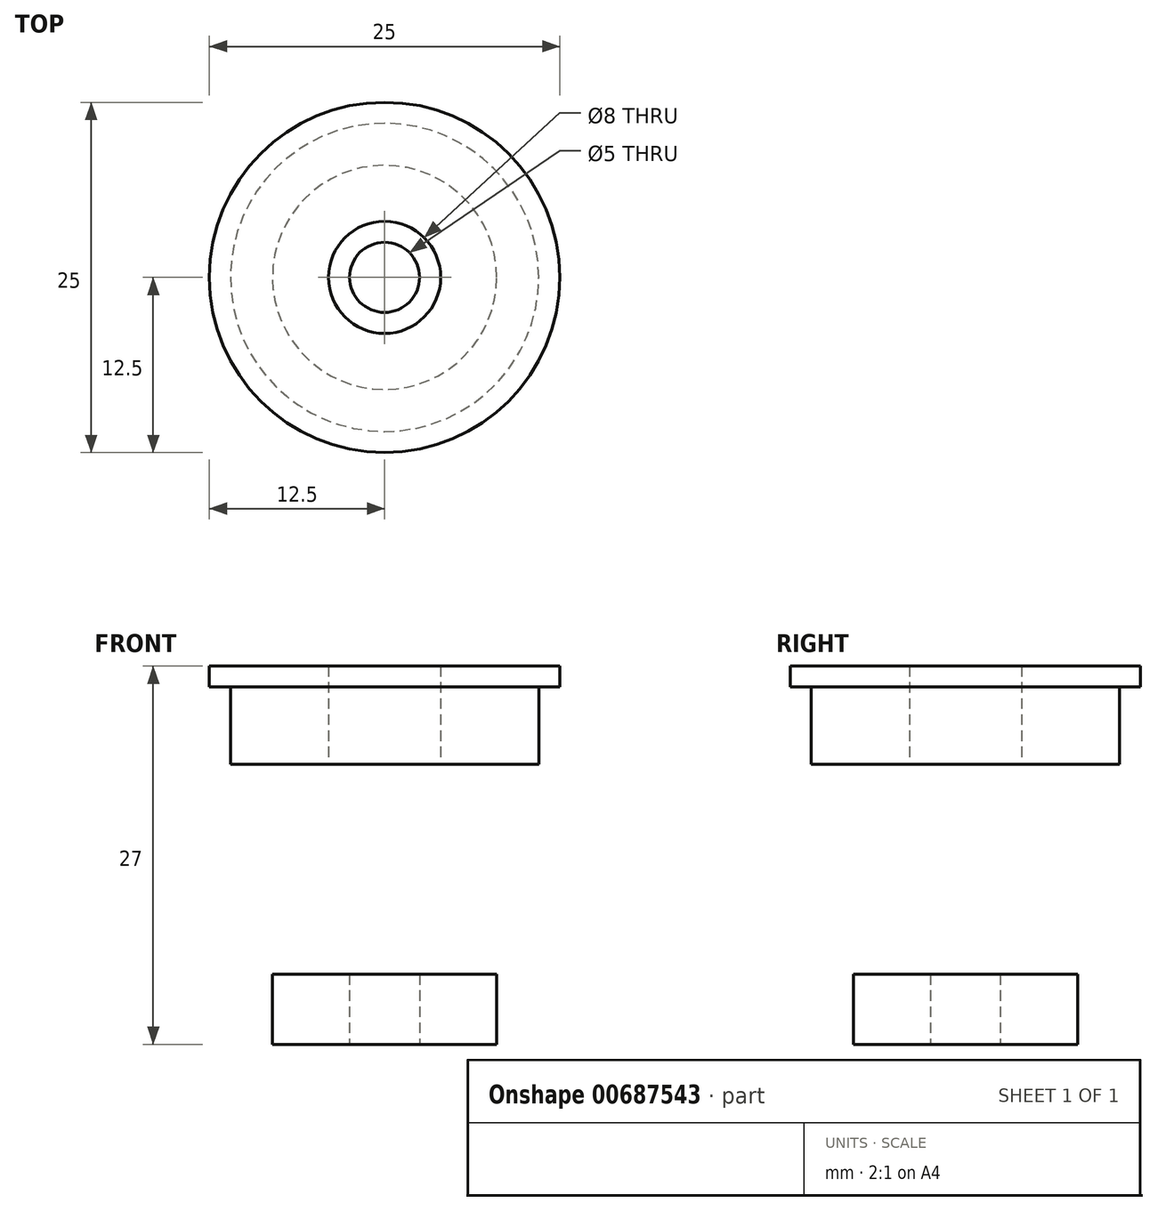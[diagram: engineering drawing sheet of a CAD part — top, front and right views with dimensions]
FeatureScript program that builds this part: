
annotation { "Feature Type Name" : "Feature", "Feature Type Description" : "" }
export const myFeature = defineFeature(function(context is Context, id is Id, definition is map)
    precondition{}
    {
        {
            var Q0;
            Q0=qCreatedBy(makeId("Front.planeOp"),FACE);
            var sketch = newSketch(context, id + "F0", { "sketchPlane" : qUnion([Q0])});
            skLineSegment(sketch, "E0", {"start": v(0, 0) * mm, "end": v(0, 7.51) * mm, "construction": true});
            skLineSegment(sketch, "E1", {"start": v(4, 0) * mm, "end": v(11, 0) * mm});
            skLineSegment(sketch, "E2", {"start": v(11, 0) * mm, "end": v(11, 5.5) * mm});
            skLineSegment(sketch, "E3", {"start": v(11, 5.5) * mm, "end": v(12.5, 5.5) * mm});
            skLineSegment(sketch, "E4", {"start": v(12.5, 5.5) * mm, "end": v(12.5, 7) * mm});
            skLineSegment(sketch, "E5", {"start": v(12.5, 7) * mm, "end": v(4, 7) * mm});
            skLineSegment(sketch, "E6", {"start": v(4, 7) * mm, "end": v(4, 0) * mm});
            skLineSegment(sketch, "E7.bottom", {"start": v(2.5, -15) * mm, "end": v(8, -15) * mm});
            skLineSegment(sketch, "E7.top", {"start": v(2.5, -20) * mm, "end": v(8, -20) * mm});
            skLineSegment(sketch, "E7.left", {"start": v(2.5, -15) * mm, "end": v(2.5, -20) * mm});
            skLineSegment(sketch, "E7.right", {"start": v(8, -15) * mm, "end": v(8, -20) * mm});
            skSolve(sketch);
        }
        {
            var Q0;
            Q0 = qSketchRegion(id + "F0", true);
            var Q1;
            Q1=sQuery(id+"F0.wireOp",EDGE,"E0");
            revolve(context, id + "F1", {"surfaceOperationType" : NewSurfaceOperationType.NEW, "entities" : qUnion([Q0]), "axis" : qUnion([Q1]), "revolveType" : RevolveType.FULL});
        }
    });
